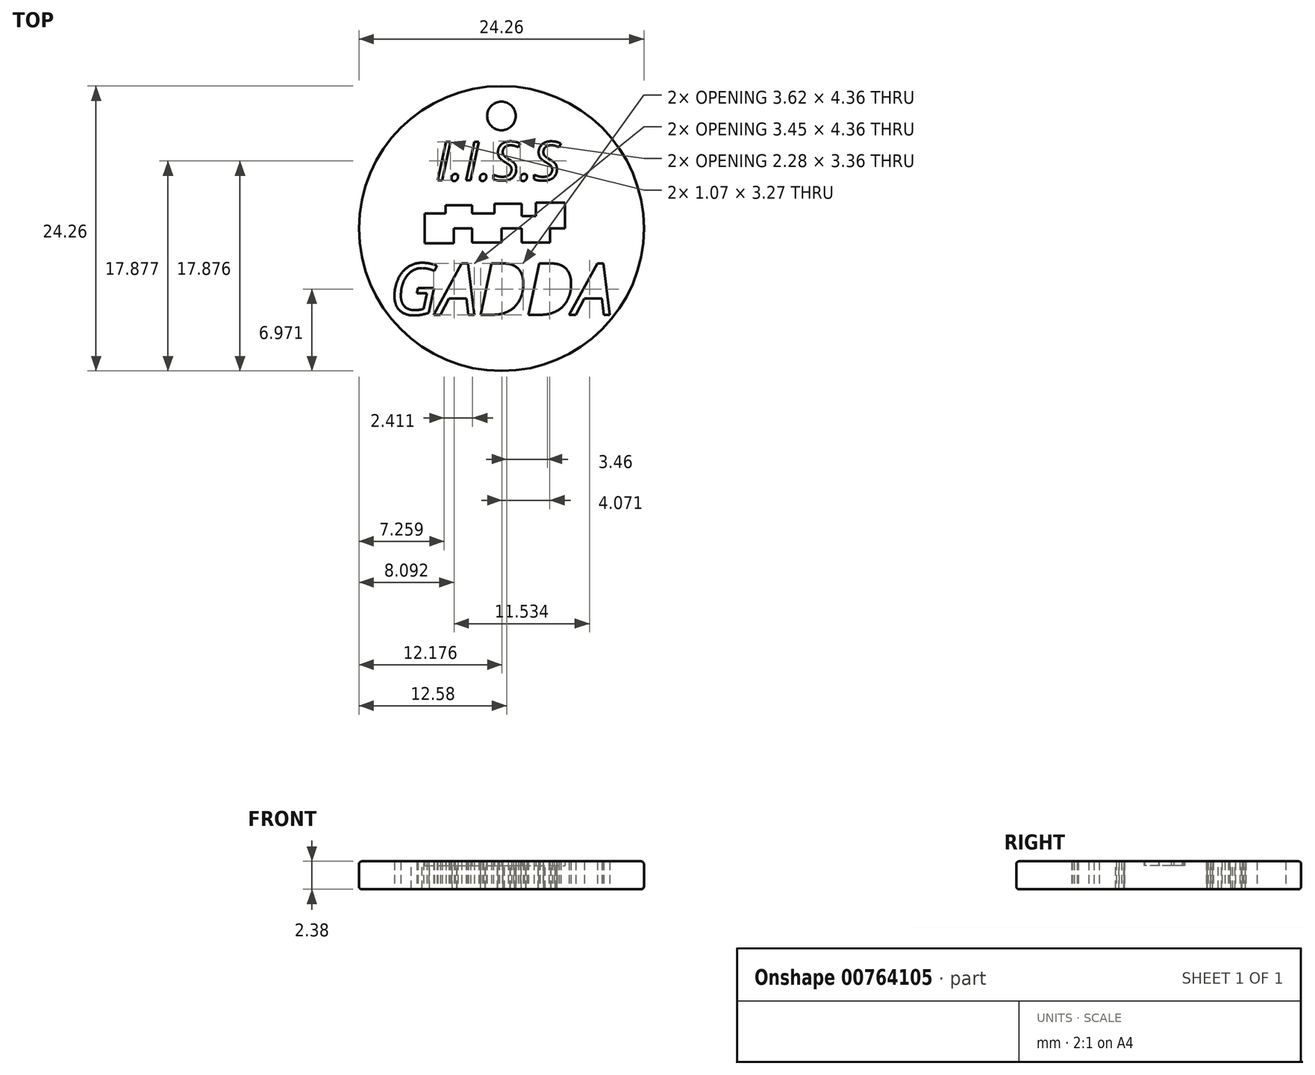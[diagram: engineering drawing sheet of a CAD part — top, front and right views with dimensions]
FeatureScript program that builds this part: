
annotation { "Feature Type Name" : "Feature", "Feature Type Description" : "" }
export const myFeature = defineFeature(function(context is Context, id is Id, definition is map)
    precondition{}
    {
        {
            var Q0;
            Q0=qCreatedBy(makeId("Top.planeOp"),FACE);
            var sketch = newSketch(context, id + "F0", { "sketchPlane" : qUnion([Q0])});
            skCircle(sketch, "E0", {"center": v(0, 0) * mm, "radius": 12.12 * mm});
            skText(sketch, "E1", { "text": "I.I.S.S", "fontName": "OpenSans-Italic.ttf"});
            skText(sketch, "E2", { "text": "GADDA", "fontName": "OpenSans-Italic.ttf"});
            skLineSegment(sketch, "E3.bottom", {"start": v(-6.53, 1.28) * mm, "end": v(-4.06, 1.28) * mm});
            skLineSegment(sketch, "E3.top", {"start": v(-6.53, -1.27) * mm, "end": v(-4.06, -1.27) * mm});
            skLineSegment(sketch, "E3.left", {"start": v(-6.53, 1.28) * mm, "end": v(-6.53, -1.27) * mm});
            skLineSegment(sketch, "E3.right", {"start": v(-4.06, 1.28) * mm, "end": v(-4.06, -1.27) * mm});
            skPoint(sketch, "E4.oppositeSnap0", {"position": v(-4.06, 0) * mm});
            skLineSegment(sketch, "E4.bottom", {"start": v(-4.76, 1.98) * mm, "end": v(-2.5, 1.98) * mm});
            skLineSegment(sketch, "E4.top", {"start": v(-4.76, 0) * mm, "end": v(-2.5, 0) * mm});
            skLineSegment(sketch, "E4.left", {"start": v(-4.76, 1.98) * mm, "end": v(-4.76, 0) * mm});
            skLineSegment(sketch, "E4.right", {"start": v(-2.5, 1.98) * mm, "end": v(-2.5, 0) * mm});
            skLineSegment(sketch, "E5.bottom", {"start": v(-2.5, 1.28) * mm, "end": v(0, 1.28) * mm});
            skLineSegment(sketch, "E5.top", {"start": v(-2.5, -1.2) * mm, "end": v(0, -1.2) * mm});
            skLineSegment(sketch, "E5.left", {"start": v(-2.5, 1.28) * mm, "end": v(-2.5, -1.2) * mm});
            skLineSegment(sketch, "E5.right", {"start": v(0, 1.28) * mm, "end": v(0, -1.2) * mm});
            skLineSegment(sketch, "E6.bottom", {"start": v(-0.6, 2.12) * mm, "end": v(1.73, 2.12) * mm});
            skLineSegment(sketch, "E6.top", {"start": v(-0.6, 0) * mm, "end": v(1.73, 0) * mm});
            skLineSegment(sketch, "E6.left", {"start": v(-0.6, 2.12) * mm, "end": v(-0.6, 0) * mm});
            skLineSegment(sketch, "E6.right", {"start": v(1.73, 2.12) * mm, "end": v(1.73, 0) * mm});
            skLineSegment(sketch, "E7.bottom", {"start": v(1.73, 1.06) * mm, "end": v(4.13, 1.06) * mm});
            skLineSegment(sketch, "E7.top", {"start": v(1.73, -1.2) * mm, "end": v(4.13, -1.2) * mm});
            skLineSegment(sketch, "E7.left", {"start": v(1.73, 1.06) * mm, "end": v(1.73, -1.2) * mm});
            skLineSegment(sketch, "E7.right", {"start": v(4.13, 1.06) * mm, "end": v(4.13, -1.2) * mm});
            skPoint(sketch, "E8.firstSnap0", {"position": v(2.93, 1.06) * mm});
            skLineSegment(sketch, "E8.bottom", {"start": v(2.93, 2.2) * mm, "end": v(5.4, 2.2) * mm});
            skLineSegment(sketch, "E8.top", {"start": v(2.93, 0) * mm, "end": v(5.4, 0) * mm});
            skLineSegment(sketch, "E8.left", {"start": v(2.93, 2.2) * mm, "end": v(2.93, 0) * mm});
            skLineSegment(sketch, "E8.right", {"start": v(5.4, 2.2) * mm, "end": v(5.4, 0) * mm});
            skCircle(sketch, "E9", {"center": v(0, 9.59) * mm, "radius": 1.22 * mm});
            const initialGuessF0  = {"E1": [-0.0056, 0.00411, 1, 0, 0.0033], "E2": [-0.00955, -0.00734, 1, 0, 0.0044]};
            skSetInitialGuess(sketch, initialGuessF0);
            skSolve(sketch);
        }
        {
            var Q0;
            Q0 = qSketchRegion(id + "F0", true);
            extrude(context, id + "F1", {"entities" : qUnion([Q0]), "depth" : 2.38 * mm, "offsetDistance" : 25 * mm});
        }
        {
            var Q0;
            Q0=makeQuery(id+"F1.opExtrude","CAP_EDGE",EDGE,{"disambiguationData":[OSD([sQuery(id+"F0.wireOp",EDGE,"E0")])],"isStart":false});
            var Q1;
            Q1=makeQuery(id+"F1.opExtrude","CAP_EDGE",EDGE,{"disambiguationData":[OSD([sQuery(id+"F0.wireOp",EDGE,"E0")])],"isStart":true});
            fillet(context, id + "F2", {"entities" : qUnion([Q0, Q1]), "radius" : .25 * mm, "tangentPropagation" : true, "allowEdgeOverflow" : false});
        }
        {
            var Q0;
            {var subQ1=sQuery(id+"F0.wireOp",EDGE,"E3.top");Q0=makeQuery(id+"F0.imprint","IMPRINT",FACE,{"disambiguationData":[TD([[makeQuery(id+"F0.imprint","IMPRINT",EDGE,{"derivedFrom":subQ1}),1.0]])]});}
            var Q1;
            {var subQ8=sQuery(id+"F0.wireOp",EDGE,"E4.bottom");Q1=makeQuery(id+"F0.imprint","IMPRINT",FACE,{"disambiguationData":[TD([[makeQuery(id+"F0.imprint","IMPRINT",EDGE,{"derivedFrom":subQ8}),-1.0]])]});}
            var Q2;
            {var subQ2=sQuery(id+"F0.wireOp",EDGE,"E5.top");Q2=makeQuery(id+"F0.imprint","IMPRINT",FACE,{"disambiguationData":[TD([[makeQuery(id+"F0.imprint","IMPRINT",EDGE,{"derivedFrom":subQ2}),1.0]])]});}
            var Q3;
            {var subQ5=sQuery(id+"F0.wireOp",EDGE,"E6.bottom");Q3=makeQuery(id+"F0.imprint","IMPRINT",FACE,{"disambiguationData":[TD([[makeQuery(id+"F0.imprint","IMPRINT",EDGE,{"derivedFrom":subQ5}),-1.0]])]});}
            var Q4;
            {var subQ2=sQuery(id+"F0.wireOp",EDGE,"E7.top");Q4=makeQuery(id+"F0.imprint","IMPRINT",FACE,{"disambiguationData":[TD([[makeQuery(id+"F0.imprint","IMPRINT",EDGE,{"derivedFrom":subQ2}),1.0]])]});}
            var Q5;
            {var subQ4=sQuery(id+"F0.wireOp",EDGE,"E8.bottom");Q5=makeQuery(id+"F0.imprint","IMPRINT",FACE,{"disambiguationData":[TD([[makeQuery(id+"F0.imprint","IMPRINT",EDGE,{"derivedFrom":subQ4}),-1.0]])]});}
            var Q6;
            {var subQ0=sQuery(id+"F0.wireOp",EDGE,"E3.right");var subQ1=sQuery(id+"F0.wireOp",EDGE,"E3.bottom");var subQ2=makeQuery(id+"F0.imprint","INTERSECT",VERTEX,{"derivedFrom":[subQ1,subQ0]});Q6=makeQuery(id+"F0.imprint","IMPRINT",FACE,{"disambiguationData":[TD([[makeQuery(id+"F0.imprint","IMPRINT",EDGE,{"disambiguationData":[TD([[subQ2,1.0]])],"derivedFrom":subQ1}),-1.0]])]});}
            var Q7;
            {var subQ0=sQuery(id+"F0.wireOp",EDGE,"E5.right");var subQ1=sQuery(id+"F0.wireOp",EDGE,"E5.bottom");var subQ2=makeQuery(id+"F0.imprint","INTERSECT",VERTEX,{"derivedFrom":[subQ1,subQ0]});Q7=makeQuery(id+"F0.imprint","IMPRINT",FACE,{"disambiguationData":[TD([[makeQuery(id+"F0.imprint","IMPRINT",EDGE,{"disambiguationData":[TD([[subQ2,1.0]])],"derivedFrom":subQ1}),-1.0]])]});}
            var Q8;
            {var subQ0=sQuery(id+"F0.wireOp",EDGE,"E7.right");var subQ1=sQuery(id+"F0.wireOp",EDGE,"E7.bottom");var subQ2=makeQuery(id+"F0.imprint","INTERSECT",VERTEX,{"derivedFrom":[subQ1,subQ0]});Q8=makeQuery(id+"F0.imprint","IMPRINT",FACE,{"disambiguationData":[TD([[makeQuery(id+"F0.imprint","IMPRINT",EDGE,{"disambiguationData":[TD([[subQ2,1.0]])],"derivedFrom":subQ1}),-1.0]])]});}
            extrude(context, id + "F3", {"entities" : qUnion([Q0, Q1, Q2, Q3, Q4, Q5, Q6, Q7, Q8]), "operationType" : NewBodyOperationType.ADD, "depth" : 2 * mm, "offsetDistance" : 25 * mm});
        }
    });
